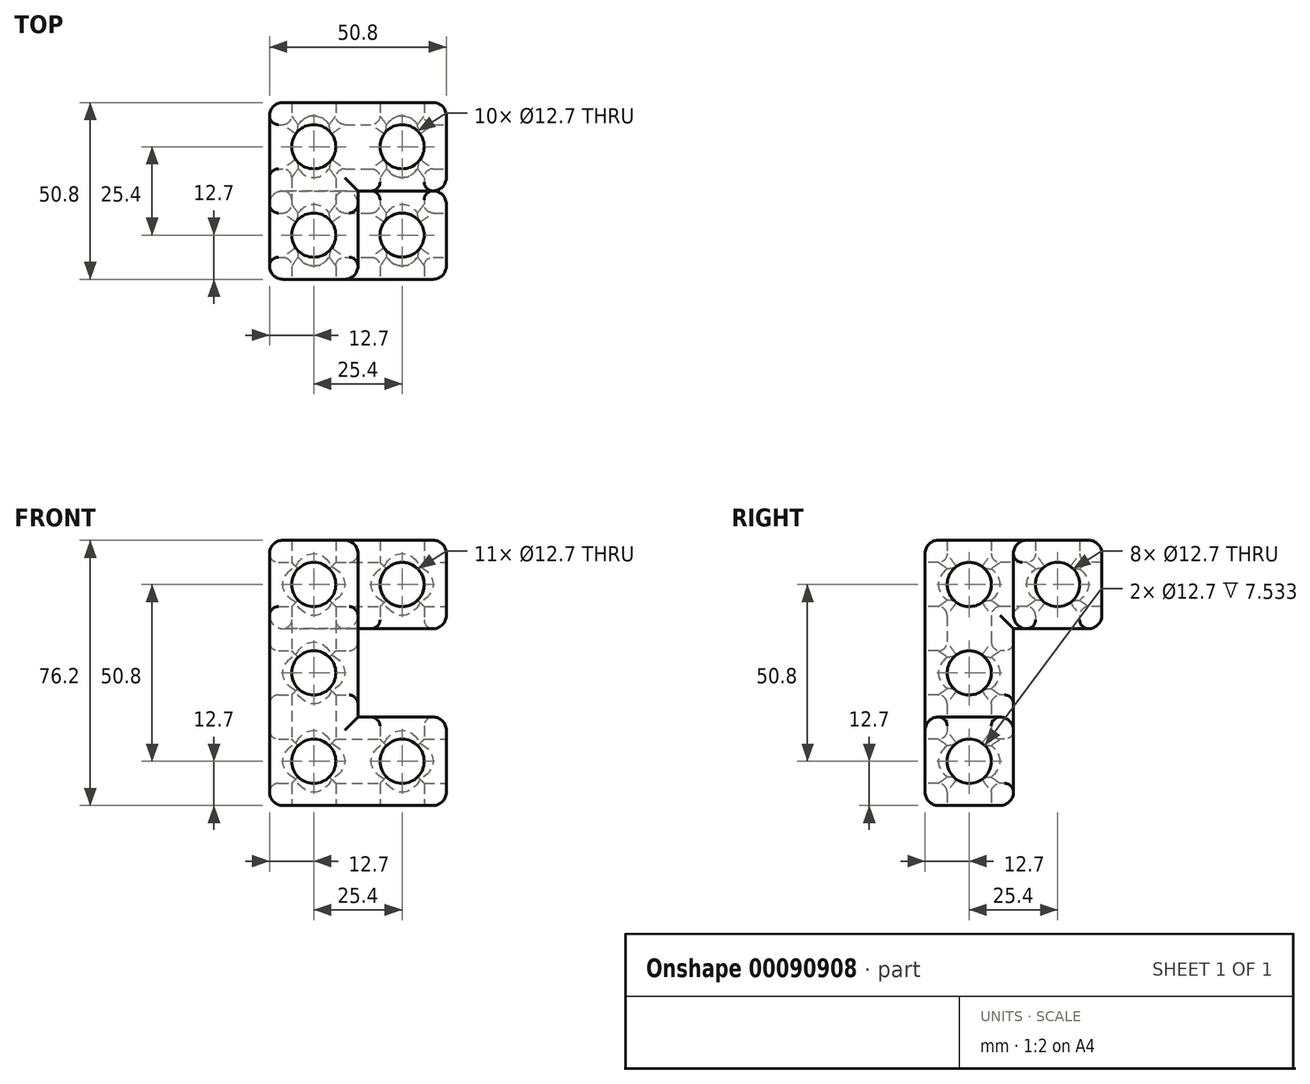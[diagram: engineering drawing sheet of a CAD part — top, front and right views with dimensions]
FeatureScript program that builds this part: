
annotation { "Feature Type Name" : "Feature", "Feature Type Description" : "" }
export const myFeature = defineFeature(function(context is Context, id is Id, definition is map)
    precondition{}
    {
        {
            var Q0;
            Q0=qCreatedBy(makeId("Top.planeOp"),FACE);
            var sketch = newSketch(context, id + "F0", { "sketchPlane" : qUnion([Q0])});
            skLineSegment(sketch, "E0.bottom", {"start": v(0, 0) * mm, "end": v(50.8, 0) * mm});
            skLineSegment(sketch, "E0.top", {"start": v(0, 25.4) * mm, "end": v(50.8, 25.4) * mm});
            skLineSegment(sketch, "E0.left", {"start": v(0, 0) * mm, "end": v(0, 25.4) * mm});
            skLineSegment(sketch, "E0.right", {"start": v(50.8, 0) * mm, "end": v(50.8, 25.4) * mm});
            skSolve(sketch);
        }
        {
            var Q0;
            Q0 = qSketchRegion(id + "F0", true);
            extrude(context, id + "F1", {"entities" : qUnion([Q0]), "depth" : 25.4 * mm});
        }
        {
            var Q0;
            Q0=makeQuery(id+"F1.opExtrude","CAP_FACE",FACE,{"disambiguationData":[OSD([sQuery(id+"F0.wireOp",EDGE,"E0.bottom"),sQuery(id+"F0.wireOp",EDGE,"E0.top"),sQuery(id+"F0.wireOp",EDGE,"E0.left"),sQuery(id+"F0.wireOp",EDGE,"E0.right")])],"isStart":false});
            var sketch = newSketch(context, id + "F2", { "sketchPlane" : qUnion([Q0])});
            skLineSegment(sketch, "E1.bottom", {"start": v(0, 0) * mm, "end": v(25.4, 0) * mm});
            skLineSegment(sketch, "E1.top", {"start": v(0, 25.4) * mm, "end": v(25.4, 25.4) * mm});
            skLineSegment(sketch, "E1.left", {"start": v(0, 0) * mm, "end": v(0, 25.4) * mm});
            skLineSegment(sketch, "E1.right", {"start": v(25.4, 0) * mm, "end": v(25.4, 25.4) * mm});
            skSolve(sketch);
        }
        {
            var Q0;
            Q0 = qSketchRegion(id + "F2", true);
            extrude(context, id + "F3", {"entities" : qUnion([Q0]), "operationType" : NewBodyOperationType.ADD, "depth" : 25.4 * mm});
        }
        {
            var Q0;
            Q0=makeQuery(id+"F3.opExtrude","CAP_FACE",FACE,{"disambiguationData":[OSD([sQuery(id+"F2.wireOp",EDGE,"E1.bottom"),sQuery(id+"F2.wireOp",EDGE,"E1.top"),sQuery(id+"F2.wireOp",EDGE,"E1.left"),sQuery(id+"F2.wireOp",EDGE,"E1.right")])],"isStart":false});
            var sketch = newSketch(context, id + "F4", { "sketchPlane" : qUnion([Q0])});
            skLineSegment(sketch, "E2.left", {"start": v(0, 0) * mm, "end": v(0, 50.8) * mm});
            skLineSegment(sketch, "E3", {"start": v(50.8, 25.4) * mm, "end": v(25.4, 25.4) * mm});
            skLineSegment(sketch, "E4", {"start": v(0, 50.8) * mm, "end": v(18.8, 50.8) * mm});
            skLineSegment(sketch, "E5", {"start": v(18.8, 50.8) * mm, "end": v(50.8, 50.8) * mm});
            skLineSegment(sketch, "E6", {"start": v(50.8, 50.8) * mm, "end": v(50.8, 25.4) * mm});
            skLineSegment(sketch, "E7", {"start": v(25.4, 25.4) * mm, "end": v(25.4, 0) * mm});
            skLineSegment(sketch, "E8", {"start": v(0, 0) * mm, "end": v(25.4, 0) * mm});
            skSolve(sketch);
        }
        {
            var Q0;
            Q0 = qSketchRegion(id + "F4", true);
            extrude(context, id + "F5", {"entities" : qUnion([Q0]), "operationType" : NewBodyOperationType.ADD, "depth" : 25.4 * mm});
        }
        {
            var Q0;
            Q0=makeQuery(id+"F5.boolean.opBoolean","MERGE",FACE,{"derivedFrom":[makeQuery(id+"F3.boolean.opBoolean","MERGE",FACE,{"derivedFrom":[makeQuery(id+"F1.opExtrude","SWEPT_FACE",FACE,{"disambiguationData":[OSD([sQuery(id+"F0.wireOp",EDGE,"E0.bottom")])]}),makeQuery(id+"F3.opExtrude","SWEPT_FACE",FACE,{"disambiguationData":[OSD([sQuery(id+"F2.wireOp",EDGE,"E1.bottom")])]})]}),makeQuery(id+"F5.opExtrude","SWEPT_FACE",FACE,{"disambiguationData":[OSD([sQuery(id+"F4.wireOp",EDGE,"E8")])]})]});
            var sketch = newSketch(context, id + "F6", { "sketchPlane" : qUnion([Q0])});
            skCircle(sketch, "E9", {"center": v(12.7, 63.5) * mm, "radius": 6.35 * mm});
            skLineSegment(sketch, "E10.direction1", {"start": v(12.7, 63.5) * mm, "end": v(38.1, 63.5) * mm, "construction": true});
            skCircle(sketch, "E11.0.1.0", {"center": v(12.7, 38.1) * mm, "radius": 6.35 * mm});
            skCircle(sketch, "E11.0.2.0", {"center": v(12.7, 12.7) * mm, "radius": 6.35 * mm});
            skCircle(sketch, "E11.1.0.0", {"center": v(38.1, 63.5) * mm, "radius": 6.35 * mm});
            skCircle(sketch, "E11.1.1.0", {"center": v(38.1, 38.1) * mm, "radius": 6.35 * mm});
            skCircle(sketch, "E11.1.2.0", {"center": v(38.1, 12.7) * mm, "radius": 6.35 * mm});
            skLineSegment(sketch, "E11.direction2", {"start": v(12.7, 63.5) * mm, "end": v(12.7, 38.1) * mm, "construction": true});
            skSolve(sketch);
        }
        {
            var Q0;
            Q0 = qSketchRegion(id + "F6", true);
            extrude(context, id + "F7", {"entities" : qUnion([Q0]), "operationType" : NewBodyOperationType.REMOVE, "oppositeDirection" : true, "depth" : 50.8 * mm});
        }
        {
            var Q0;
            Q0=makeQuery(id+"F5.opExtrude","SWEPT_FACE",FACE,{"disambiguationData":[OSD([sQuery(id+"F4.wireOp",EDGE,"E6")])]});
            var sketch = newSketch(context, id + "F8", { "sketchPlane" : qUnion([Q0])});
            skCircle(sketch, "E12", {"center": v(12.7, 63.5) * mm, "radius": 6.35 * mm});
            skCircle(sketch, "E13.0.1.0", {"center": v(12.7, 38.1) * mm, "radius": 6.35 * mm});
            skCircle(sketch, "E13.0.2.0", {"center": v(12.7, 12.7) * mm, "radius": 6.35 * mm});
            skCircle(sketch, "E13.1.0.0", {"center": v(38.1, 63.5) * mm, "radius": 6.35 * mm});
            skCircle(sketch, "E13.1.1.0", {"center": v(38.1, 38.1) * mm, "radius": 6.35 * mm});
            skCircle(sketch, "E13.1.2.0", {"center": v(38.1, 12.7) * mm, "radius": 6.35 * mm});
            skLineSegment(sketch, "E13.direction1", {"start": v(12.7, 63.5) * mm, "end": v(38.1, 63.5) * mm, "construction": true});
            skLineSegment(sketch, "E13.direction2", {"start": v(12.7, 63.5) * mm, "end": v(12.7, 38.1) * mm, "construction": true});
            skSolve(sketch);
        }
        {
            var Q0;
            Q0 = qSketchRegion(id + "F8", true);
            extrude(context, id + "F9", {"entities" : qUnion([Q0]), "operationType" : NewBodyOperationType.REMOVE, "oppositeDirection" : true, "depth" : 76.2 * mm});
        }
        {
            var Q0;
            Q0=makeQuery(id+"F1.opExtrude","CAP_FACE",FACE,{"disambiguationData":[OSD([sQuery(id+"F0.wireOp",EDGE,"E0.bottom"),sQuery(id+"F0.wireOp",EDGE,"E0.top"),sQuery(id+"F0.wireOp",EDGE,"E0.left"),sQuery(id+"F0.wireOp",EDGE,"E0.right")])],"isStart":true});
            var sketch = newSketch(context, id + "F10", { "sketchPlane" : qUnion([Q0])});
            skCircle(sketch, "E14", {"center": v(12.7, -12.7) * mm, "radius": 6.35 * mm});
            skCircle(sketch, "E15.0.1.0", {"center": v(12.7, -38.1) * mm, "radius": 6.35 * mm});
            skCircle(sketch, "E15.1.0.0", {"center": v(38.1, -12.7) * mm, "radius": 6.35 * mm});
            skCircle(sketch, "E15.1.1.0", {"center": v(38.1, -38.1) * mm, "radius": 6.35 * mm});
            skLineSegment(sketch, "E15.direction1", {"start": v(12.7, -12.7) * mm, "end": v(38.1, -12.7) * mm, "construction": true});
            skLineSegment(sketch, "E15.direction2", {"start": v(12.7, -12.7) * mm, "end": v(12.7, -38.1) * mm, "construction": true});
            skSolve(sketch);
        }
        {
            var Q0;
            Q0 = qSketchRegion(id + "F10", true);
            extrude(context, id + "F11", {"entities" : qUnion([Q0]), "operationType" : NewBodyOperationType.REMOVE, "oppositeDirection" : true, "depth" : 76.2 * mm});
        }
        {
            var Q0;
            Q0=makeQuery(id+"F11.boolean.opBoolean","COPY",EDGE,{"derivedFrom":makeQuery(id+"F11.opExtrude","CAP_EDGE",EDGE,{"disambiguationData":[OSD([sQuery(id+"F10.wireOp",EDGE,"E15.1.1.0")])],"isStart":false})});
            var Q1;
            Q1=makeQuery(id+"F11.boolean.opBoolean","COPY",EDGE,{"derivedFrom":makeQuery(id+"F11.opExtrude","CAP_EDGE",EDGE,{"disambiguationData":[OSD([sQuery(id+"F10.wireOp",EDGE,"E15.0.1.0")])],"isStart":false})});
            var Q2;
            Q2=makeQuery(id+"F11.boolean.opBoolean","COPY",EDGE,{"derivedFrom":makeQuery(id+"F11.opExtrude","CAP_EDGE",EDGE,{"disambiguationData":[OSD([sQuery(id+"F10.wireOp",EDGE,"E14")])],"isStart":false})});
            var Q3;
            Q3=makeQuery(id+"F11.boolean.opBoolean","INTERSECT",EDGE,{"derivedFrom":[makeQuery(id+"F1.opExtrude","CAP_FACE",FACE,{"disambiguationData":[OSD([sQuery(id+"F0.wireOp",EDGE,"E0.bottom"),sQuery(id+"F0.wireOp",EDGE,"E0.top"),sQuery(id+"F0.wireOp",EDGE,"E0.left"),sQuery(id+"F0.wireOp",EDGE,"E0.right")])],"isStart":false}),makeQuery(id+"F11.opExtrude","SWEPT_FACE",FACE,{"disambiguationData":[OSD([sQuery(id+"F10.wireOp",EDGE,"E15.1.0.0")])]})]});
            var Q4;
            Q4=makeQuery(id+"F9.boolean.opBoolean","INTERSECT",EDGE,{"derivedFrom":[makeQuery(id+"F5.boolean.opBoolean","MERGE",FACE,{"derivedFrom":[makeQuery(id+"F3.opExtrude","SWEPT_FACE",FACE,{"disambiguationData":[OSD([sQuery(id+"F2.wireOp",EDGE,"E1.right")])]}),makeQuery(id+"F5.opExtrude","SWEPT_FACE",FACE,{"disambiguationData":[OSD([sQuery(id+"F4.wireOp",EDGE,"E7")])]})]}),makeQuery(id+"F9.opExtrude","SWEPT_FACE",FACE,{"disambiguationData":[OSD([sQuery(id+"F8.wireOp",EDGE,"E13.0.1.0")])]})]});
            var Q5;
            Q5=makeQuery(id+"F7.boolean.opBoolean","INTERSECT",EDGE,{"derivedFrom":[makeQuery(id+"F5.opExtrude","SWEPT_FACE",FACE,{"disambiguationData":[OSD([sQuery(id+"F4.wireOp",EDGE,"E3")])]}),makeQuery(id+"F7.opExtrude","SWEPT_FACE",FACE,{"disambiguationData":[OSD([sQuery(id+"F6.wireOp",EDGE,"E11.1.0.0")])]})]});
            var Q6;
            Q6=makeQuery(id+"F9.boolean.opBoolean","COPY",EDGE,{"derivedFrom":makeQuery(id+"F9.opExtrude","CAP_EDGE",EDGE,{"disambiguationData":[OSD([sQuery(id+"F8.wireOp",EDGE,"E13.1.0.0")])],"isStart":true})});
            var Q7;
            Q7=makeQuery(id+"F9.boolean.opBoolean","INTERSECT",EDGE,{"derivedFrom":[makeQuery(id+"F5.boolean.opBoolean","MERGE",FACE,{"derivedFrom":[makeQuery(id+"F3.opExtrude","SWEPT_FACE",FACE,{"disambiguationData":[OSD([sQuery(id+"F2.wireOp",EDGE,"E1.right")])]}),makeQuery(id+"F5.opExtrude","SWEPT_FACE",FACE,{"disambiguationData":[OSD([sQuery(id+"F4.wireOp",EDGE,"E7")])]})]}),makeQuery(id+"F9.opExtrude","SWEPT_FACE",FACE,{"disambiguationData":[OSD([sQuery(id+"F8.wireOp",EDGE,"E12")])]})]});
            var Q8;
            Q8=makeQuery(id+"F9.boolean.opBoolean","COPY",EDGE,{"derivedFrom":makeQuery(id+"F9.opExtrude","CAP_EDGE",EDGE,{"disambiguationData":[OSD([sQuery(id+"F8.wireOp",EDGE,"E13.0.2.0")])],"isStart":true})});
            var Q9;
            Q9=makeQuery(id+"F7.boolean.opBoolean","COPY",EDGE,{"derivedFrom":makeQuery(id+"F7.opExtrude","CAP_EDGE",EDGE,{"disambiguationData":[OSD([sQuery(id+"F6.wireOp",EDGE,"E11.0.2.0")])],"isStart":true})});
            var Q10;
            Q10=makeQuery(id+"F7.boolean.opBoolean","COPY",EDGE,{"derivedFrom":makeQuery(id+"F7.opExtrude","CAP_EDGE",EDGE,{"disambiguationData":[OSD([sQuery(id+"F6.wireOp",EDGE,"E11.0.1.0")])],"isStart":true})});
            var Q11;
            Q11=makeQuery(id+"F7.boolean.opBoolean","COPY",EDGE,{"derivedFrom":makeQuery(id+"F7.opExtrude","CAP_EDGE",EDGE,{"disambiguationData":[OSD([sQuery(id+"F6.wireOp",EDGE,"E9")])],"isStart":true})});
            var Q12;
            Q12=makeQuery(id+"F7.boolean.opBoolean","COPY",EDGE,{"derivedFrom":makeQuery(id+"F7.opExtrude","CAP_EDGE",EDGE,{"disambiguationData":[OSD([sQuery(id+"F6.wireOp",EDGE,"E11.1.2.0")])],"isStart":true})});
            var Q13;
            Q13=makeQuery(id+"F9.boolean.opBoolean","INTERSECT",EDGE,{"derivedFrom":[makeQuery(id+"F5.boolean.opBoolean","MERGE",FACE,{"derivedFrom":[makeQuery(id+"F3.boolean.opBoolean","MERGE",FACE,{"derivedFrom":[makeQuery(id+"F1.opExtrude","SWEPT_FACE",FACE,{"disambiguationData":[OSD([sQuery(id+"F0.wireOp",EDGE,"E0.left")])]}),makeQuery(id+"F3.opExtrude","SWEPT_FACE",FACE,{"disambiguationData":[OSD([sQuery(id+"F2.wireOp",EDGE,"E1.left")])]})]}),makeQuery(id+"F5.opExtrude","SWEPT_FACE",FACE,{"disambiguationData":[OSD([sQuery(id+"F4.wireOp",EDGE,"E2.left")])]})]}),makeQuery(id+"F9.opExtrude","SWEPT_FACE",FACE,{"disambiguationData":[OSD([sQuery(id+"F8.wireOp",EDGE,"E12")])]})]});
            var Q14;
            Q14=makeQuery(id+"F9.boolean.opBoolean","INTERSECT",EDGE,{"derivedFrom":[makeQuery(id+"F5.boolean.opBoolean","MERGE",FACE,{"derivedFrom":[makeQuery(id+"F3.boolean.opBoolean","MERGE",FACE,{"derivedFrom":[makeQuery(id+"F1.opExtrude","SWEPT_FACE",FACE,{"disambiguationData":[OSD([sQuery(id+"F0.wireOp",EDGE,"E0.left")])]}),makeQuery(id+"F3.opExtrude","SWEPT_FACE",FACE,{"disambiguationData":[OSD([sQuery(id+"F2.wireOp",EDGE,"E1.left")])]})]}),makeQuery(id+"F5.opExtrude","SWEPT_FACE",FACE,{"disambiguationData":[OSD([sQuery(id+"F4.wireOp",EDGE,"E2.left")])]})]}),makeQuery(id+"F9.opExtrude","SWEPT_FACE",FACE,{"disambiguationData":[OSD([sQuery(id+"F8.wireOp",EDGE,"E13.1.0.0")])]})]});
            var Q15;
            Q15=makeQuery(id+"F11.boolean.opBoolean","INTERSECT",EDGE,{"derivedFrom":[makeQuery(id+"F5.opExtrude","CAP_FACE",FACE,{"disambiguationData":[OSD([sQuery(id+"F4.wireOp",EDGE,"E2.left"),sQuery(id+"F4.wireOp",EDGE,"E3"),sQuery(id+"F4.wireOp",EDGE,"E4"),sQuery(id+"F4.wireOp",EDGE,"E5"),sQuery(id+"F4.wireOp",EDGE,"E6"),sQuery(id+"F4.wireOp",EDGE,"E8"),sQuery(id+"F4.wireOp",EDGE,"E7")])],"isStart":true}),makeQuery(id+"F11.opExtrude","SWEPT_FACE",FACE,{"disambiguationData":[OSD([sQuery(id+"F10.wireOp",EDGE,"E15.0.1.0")])]})]});
            var Q16;
            Q16=makeQuery(id+"F9.boolean.opBoolean","INTERSECT",EDGE,{"derivedFrom":[makeQuery(id+"F5.boolean.opBoolean","MERGE",FACE,{"derivedFrom":[makeQuery(id+"F3.boolean.opBoolean","MERGE",FACE,{"derivedFrom":[makeQuery(id+"F1.opExtrude","SWEPT_FACE",FACE,{"disambiguationData":[OSD([sQuery(id+"F0.wireOp",EDGE,"E0.left")])]}),makeQuery(id+"F3.opExtrude","SWEPT_FACE",FACE,{"disambiguationData":[OSD([sQuery(id+"F2.wireOp",EDGE,"E1.left")])]})]}),makeQuery(id+"F5.opExtrude","SWEPT_FACE",FACE,{"disambiguationData":[OSD([sQuery(id+"F4.wireOp",EDGE,"E2.left")])]})]}),makeQuery(id+"F9.opExtrude","SWEPT_FACE",FACE,{"disambiguationData":[OSD([sQuery(id+"F8.wireOp",EDGE,"E13.0.1.0")])]})]});
            var Q17;
            Q17=makeQuery(id+"F9.boolean.opBoolean","INTERSECT",EDGE,{"derivedFrom":[makeQuery(id+"F5.boolean.opBoolean","MERGE",FACE,{"derivedFrom":[makeQuery(id+"F3.boolean.opBoolean","MERGE",FACE,{"derivedFrom":[makeQuery(id+"F1.opExtrude","SWEPT_FACE",FACE,{"disambiguationData":[OSD([sQuery(id+"F0.wireOp",EDGE,"E0.left")])]}),makeQuery(id+"F3.opExtrude","SWEPT_FACE",FACE,{"disambiguationData":[OSD([sQuery(id+"F2.wireOp",EDGE,"E1.left")])]})]}),makeQuery(id+"F5.opExtrude","SWEPT_FACE",FACE,{"disambiguationData":[OSD([sQuery(id+"F4.wireOp",EDGE,"E2.left")])]})]}),makeQuery(id+"F9.opExtrude","SWEPT_FACE",FACE,{"disambiguationData":[OSD([sQuery(id+"F8.wireOp",EDGE,"E13.0.2.0")])]})]});
            var Q18;
            Q18=makeQuery(id+"F11.boolean.opBoolean","COPY",EDGE,{"derivedFrom":makeQuery(id+"F11.opExtrude","CAP_EDGE",EDGE,{"disambiguationData":[OSD([sQuery(id+"F10.wireOp",EDGE,"E15.1.0.0")])],"isStart":true})});
            var Q19;
            Q19=makeQuery(id+"F11.boolean.opBoolean","COPY",EDGE,{"derivedFrom":makeQuery(id+"F11.opExtrude","CAP_EDGE",EDGE,{"disambiguationData":[OSD([sQuery(id+"F10.wireOp",EDGE,"E14")])],"isStart":true})});
            var Q20;
            Q20=makeQuery(id+"F11.boolean.opBoolean","INTERSECT",EDGE,{"derivedFrom":[makeQuery(id+"F5.opExtrude","CAP_FACE",FACE,{"disambiguationData":[OSD([sQuery(id+"F4.wireOp",EDGE,"E2.left"),sQuery(id+"F4.wireOp",EDGE,"E3"),sQuery(id+"F4.wireOp",EDGE,"E4"),sQuery(id+"F4.wireOp",EDGE,"E5"),sQuery(id+"F4.wireOp",EDGE,"E6"),sQuery(id+"F4.wireOp",EDGE,"E8"),sQuery(id+"F4.wireOp",EDGE,"E7")])],"isStart":true}),makeQuery(id+"F11.opExtrude","SWEPT_FACE",FACE,{"disambiguationData":[OSD([sQuery(id+"F10.wireOp",EDGE,"E15.1.1.0")])]})]});
            var Q21;
            Q21=makeQuery(id+"F7.boolean.opBoolean","COPY",EDGE,{"derivedFrom":makeQuery(id+"F7.opExtrude","CAP_EDGE",EDGE,{"disambiguationData":[OSD([sQuery(id+"F6.wireOp",EDGE,"E9")])],"isStart":false})});
            var Q22;
            Q22=makeQuery(id+"F7.boolean.opBoolean","INTERSECT",EDGE,{"derivedFrom":[makeQuery(id+"F3.boolean.opBoolean","MERGE",FACE,{"derivedFrom":[makeQuery(id+"F1.opExtrude","SWEPT_FACE",FACE,{"disambiguationData":[OSD([sQuery(id+"F0.wireOp",EDGE,"E0.top")])]}),makeQuery(id+"F3.opExtrude","SWEPT_FACE",FACE,{"disambiguationData":[OSD([sQuery(id+"F2.wireOp",EDGE,"E1.top")])]})]}),makeQuery(id+"F7.opExtrude","SWEPT_FACE",FACE,{"disambiguationData":[OSD([sQuery(id+"F6.wireOp",EDGE,"E11.0.1.0")])]})]});
            var Q23;
            Q23=makeQuery(id+"F7.boolean.opBoolean","INTERSECT",EDGE,{"derivedFrom":[makeQuery(id+"F3.boolean.opBoolean","MERGE",FACE,{"derivedFrom":[makeQuery(id+"F1.opExtrude","SWEPT_FACE",FACE,{"disambiguationData":[OSD([sQuery(id+"F0.wireOp",EDGE,"E0.top")])]}),makeQuery(id+"F3.opExtrude","SWEPT_FACE",FACE,{"disambiguationData":[OSD([sQuery(id+"F2.wireOp",EDGE,"E1.top")])]})]}),makeQuery(id+"F7.opExtrude","SWEPT_FACE",FACE,{"disambiguationData":[OSD([sQuery(id+"F6.wireOp",EDGE,"E11.0.2.0")])]})]});
            var Q24;
            Q24=makeQuery(id+"F7.boolean.opBoolean","COPY",EDGE,{"derivedFrom":makeQuery(id+"F7.opExtrude","CAP_EDGE",EDGE,{"disambiguationData":[OSD([sQuery(id+"F6.wireOp",EDGE,"E11.1.0.0")])],"isStart":false})});
            var Q25;
            Q25=makeQuery(id+"F7.boolean.opBoolean","INTERSECT",EDGE,{"derivedFrom":[makeQuery(id+"F3.boolean.opBoolean","MERGE",FACE,{"derivedFrom":[makeQuery(id+"F1.opExtrude","SWEPT_FACE",FACE,{"disambiguationData":[OSD([sQuery(id+"F0.wireOp",EDGE,"E0.top")])]}),makeQuery(id+"F3.opExtrude","SWEPT_FACE",FACE,{"disambiguationData":[OSD([sQuery(id+"F2.wireOp",EDGE,"E1.top")])]})]}),makeQuery(id+"F7.opExtrude","SWEPT_FACE",FACE,{"disambiguationData":[OSD([sQuery(id+"F6.wireOp",EDGE,"E11.1.2.0")])]})]});
            fillet(context, id + "F12", {"entities" : qUnion([Q0, Q1, Q2, Q3, Q4, Q5, Q6, Q7, Q8, Q9, Q10, Q11, Q12, Q13, Q14, Q15, Q16, Q17, Q18, Q19, Q20, Q21, Q22, Q23, Q24, Q25]), "radius" : 2.54 * mm, "tangentPropagation" : true, "allowEdgeOverflow" : false});
        }
        {
            var Q0;
            Q0=makeQuery(id+"F5.boolean.opBoolean","MERGE",EDGE,{"derivedFrom":[makeQuery(id+"F3.boolean.opBoolean","MERGE",EDGE,{"derivedFrom":[makeQuery(id+"F1.opExtrude","SWEPT_EDGE",EDGE,{"disambiguationData":[OSD([sQuery(id+"F0.wireOp",EDGE,"E0.bottom"),sQuery(id+"F0.wireOp",EDGE,"E0.left")])]}),makeQuery(id+"F3.opExtrude","SWEPT_EDGE",EDGE,{"disambiguationData":[OSD([sQuery(id+"F2.wireOp",EDGE,"E1.bottom"),sQuery(id+"F2.wireOp",EDGE,"E1.left")])]})]}),makeQuery(id+"F5.opExtrude","SWEPT_EDGE",EDGE,{"disambiguationData":[OSD([sQuery(id+"F4.wireOp",EDGE,"E2.left"),sQuery(id+"F4.wireOp",EDGE,"E8")])]})]});
            var Q1;
            Q1=makeQuery(id+"F5.opExtrude","CAP_EDGE",EDGE,{"disambiguationData":[OSD([sQuery(id+"F4.wireOp",EDGE,"E8")])],"isStart":false});
            var Q2;
            Q2=makeQuery(id+"F5.boolean.opBoolean","MERGE",EDGE,{"derivedFrom":[makeQuery(id+"F3.opExtrude","SWEPT_EDGE",EDGE,{"disambiguationData":[OSD([sQuery(id+"F0.wireOp",EDGE,"E0.bottom"),sQuery(id+"F2.wireOp",EDGE,"E1.bottom"),sQuery(id+"F2.wireOp",EDGE,"E1.right")])]}),makeQuery(id+"F5.opExtrude","SWEPT_EDGE",EDGE,{"disambiguationData":[OSD([sQuery(id+"F4.wireOp",EDGE,"E8"),sQuery(id+"F4.wireOp",EDGE,"E7")])]})]});
            var Q3;
            Q3=makeQuery(id+"F1.opExtrude","CAP_EDGE",EDGE,{"disambiguationData":[OSD([sQuery(id+"F0.wireOp",EDGE,"E0.bottom")])],"isStart":false});
            var Q4;
            Q4=makeQuery(id+"F1.opExtrude","SWEPT_EDGE",EDGE,{"disambiguationData":[OSD([sQuery(id+"F0.wireOp",EDGE,"E0.bottom"),sQuery(id+"F0.wireOp",EDGE,"E0.right")])]});
            var Q5;
            Q5=makeQuery(id+"F1.opExtrude","CAP_EDGE",EDGE,{"disambiguationData":[OSD([sQuery(id+"F0.wireOp",EDGE,"E0.bottom")])],"isStart":true});
            var Q6;
            Q6=makeQuery(id+"F1.opExtrude","CAP_EDGE",EDGE,{"disambiguationData":[OSD([sQuery(id+"F0.wireOp",EDGE,"E0.right")])],"isStart":true});
            var Q7;
            Q7=makeQuery(id+"F1.opExtrude","CAP_EDGE",EDGE,{"disambiguationData":[OSD([sQuery(id+"F0.wireOp",EDGE,"E0.top")])],"isStart":true});
            var Q8;
            Q8=makeQuery(id+"F1.opExtrude","CAP_EDGE",EDGE,{"disambiguationData":[OSD([sQuery(id+"F0.wireOp",EDGE,"E0.left")])],"isStart":true});
            var Q9;
            Q9=makeQuery(id+"F3.boolean.opBoolean","MERGE",EDGE,{"derivedFrom":[makeQuery(id+"F1.opExtrude","SWEPT_EDGE",EDGE,{"disambiguationData":[OSD([sQuery(id+"F0.wireOp",EDGE,"E0.top"),sQuery(id+"F0.wireOp",EDGE,"E0.left")])]}),makeQuery(id+"F3.opExtrude","SWEPT_EDGE",EDGE,{"disambiguationData":[OSD([sQuery(id+"F2.wireOp",EDGE,"E1.top"),sQuery(id+"F2.wireOp",EDGE,"E1.left")])]})]});
            var Q10;
            Q10=makeQuery(id+"F5.opExtrude","CAP_EDGE",EDGE,{"disambiguationData":[OSD([sQuery(id+"F4.wireOp",EDGE,"E2.left")])],"isStart":false});
            var Q11;
            Q11=makeQuery(id+"F5.opExtrude","SWEPT_EDGE",EDGE,{"disambiguationData":[OSD([sQuery(id+"F4.wireOp",EDGE,"E2.left"),sQuery(id+"F4.wireOp",EDGE,"E4")])]});
            var Q12;
            Q12=makeQuery(id+"F5.opExtrude","CAP_EDGE",EDGE,{"disambiguationData":[OSD([sQuery(id+"F4.wireOp",EDGE,"E4"),sQuery(id+"F4.wireOp",EDGE,"E5")])],"isStart":true});
            var Q13;
            Q13=makeQuery(id+"F5.opExtrude","CAP_EDGE",EDGE,{"disambiguationData":[OSD([sQuery(id+"F4.wireOp",EDGE,"E2.left")])],"isStart":true});
            var Q14;
            Q14=makeQuery(id+"F1.opExtrude","CAP_EDGE",EDGE,{"disambiguationData":[OSD([sQuery(id+"F0.wireOp",EDGE,"E0.right")])],"isStart":false});
            var Q15;
            Q15=makeQuery(id+"F1.opExtrude","SWEPT_EDGE",EDGE,{"disambiguationData":[OSD([sQuery(id+"F0.wireOp",EDGE,"E0.top"),sQuery(id+"F0.wireOp",EDGE,"E0.right")])]});
            var Q16;
            Q16=makeQuery(id+"F1.opExtrude","CAP_EDGE",EDGE,{"disambiguationData":[OSD([sQuery(id+"F0.wireOp",EDGE,"E0.top")])],"isStart":false});
            var Q17;
            Q17=makeQuery(id+"F3.opExtrude","SWEPT_EDGE",EDGE,{"disambiguationData":[OSD([sQuery(id+"F0.wireOp",EDGE,"E0.top"),sQuery(id+"F2.wireOp",EDGE,"E1.top"),sQuery(id+"F2.wireOp",EDGE,"E1.right")])]});
            var Q18;
            Q18=makeQuery(id+"F5.opExtrude","SWEPT_EDGE",EDGE,{"disambiguationData":[OSD([sQuery(id+"F4.wireOp",EDGE,"E5"),sQuery(id+"F4.wireOp",EDGE,"E6")])]});
            var Q19;
            Q19=makeQuery(id+"F5.opExtrude","CAP_EDGE",EDGE,{"disambiguationData":[OSD([sQuery(id+"F4.wireOp",EDGE,"E4"),sQuery(id+"F4.wireOp",EDGE,"E5")])],"isStart":false});
            var Q20;
            Q20=makeQuery(id+"F5.opExtrude","CAP_EDGE",EDGE,{"disambiguationData":[OSD([sQuery(id+"F4.wireOp",EDGE,"E6")])],"isStart":false});
            var Q21;
            Q21=makeQuery(id+"F5.opExtrude","CAP_EDGE",EDGE,{"disambiguationData":[OSD([sQuery(id+"F4.wireOp",EDGE,"E7")])],"isStart":false});
            var Q22;
            Q22=makeQuery(id+"F5.opExtrude","CAP_EDGE",EDGE,{"disambiguationData":[OSD([sQuery(id+"F4.wireOp",EDGE,"E3")])],"isStart":false});
            var Q23;
            Q23=makeQuery(id+"F5.opExtrude","SWEPT_EDGE",EDGE,{"disambiguationData":[OSD([sQuery(id+"F4.wireOp",EDGE,"E3"),sQuery(id+"F4.wireOp",EDGE,"E6")])]});
            var Q24;
            Q24=makeQuery(id+"F5.opExtrude","CAP_EDGE",EDGE,{"disambiguationData":[OSD([sQuery(id+"F4.wireOp",EDGE,"E6")])],"isStart":true});
            fillet(context, id + "F13", {"entities" : qUnion([Q0, Q1, Q2, Q3, Q4, Q5, Q6, Q7, Q8, Q9, Q10, Q11, Q12, Q13, Q14, Q15, Q16, Q17, Q18, Q19, Q20, Q21, Q22, Q23, Q24]), "radius" : 3.8 * mm, "tangentPropagation" : true, "allowEdgeOverflow" : false});
        }
        {
            var Q0;
            Q0=makeQuery(id+"F5.opExtrude","CAP_EDGE",EDGE,{"disambiguationData":[OSD([sQuery(id+"F4.wireOp",EDGE,"E3")])],"isStart":true});
            var Q1;
            {var subQ0=sQuery(id+"F2.wireOp",EDGE,"E1.top");Q1=makeQuery(id+"F13.opFillet","TWEAK_EDGE",EDGE,{"derivedFrom":[makeQuery(id+"F5.boolean.opBoolean","MERGE",VERTEX,{"derivedFrom":[makeQuery(id+"F3.opExtrude","CAP_VERTEX",VERTEX,{"disambiguationData":[OSD([sQuery(id+"F0.wireOp",EDGE,"E0.top"),subQ0,sQuery(id+"F2.wireOp",EDGE,"E1.right")])],"isStart":false}),makeQuery(id+"F5.opExtrude","CAP_VERTEX",VERTEX,{"disambiguationData":[OSD([subQ0,sQuery(id+"F4.wireOp",EDGE,"E3"),sQuery(id+"F4.wireOp",EDGE,"E7")])],"isStart":true})]})]});}
            fillet(context, id + "F14", {"entities" : qUnion([Q0, Q1]), "radius" : 3.8 * mm, "tangentPropagation" : true, "allowEdgeOverflow" : false});
        }
        {
            var Q0;
            Q0=makeQuery(id+"F11.boolean.opBoolean","INTERSECT",EDGE,{"disambiguationData":[OD(0.0)],"derivedFrom":[makeQuery(id+"F9.boolean.opBoolean","COPY",FACE,{"disambiguationData":[OD(2.0)],"derivedFrom":makeQuery(id+"F9.opExtrude","SWEPT_FACE",FACE,{"disambiguationData":[OSD([sQuery(id+"F8.wireOp",EDGE,"E13.0.2.0")])]})}),makeQuery(id+"F11.opExtrude","SWEPT_FACE",FACE,{"disambiguationData":[OSD([sQuery(id+"F10.wireOp",EDGE,"E15.1.0.0")])]})]});
            var Q1;
            Q1=makeQuery(id+"F9.boolean.opBoolean","INTERSECT",EDGE,{"disambiguationData":[OD(1.0)],"derivedFrom":[makeQuery(id+"F7.boolean.opBoolean","COPY",FACE,{"derivedFrom":makeQuery(id+"F7.opExtrude","SWEPT_FACE",FACE,{"disambiguationData":[OSD([sQuery(id+"F6.wireOp",EDGE,"E11.1.2.0")])]})}),makeQuery(id+"F9.opExtrude","SWEPT_FACE",FACE,{"disambiguationData":[OSD([sQuery(id+"F8.wireOp",EDGE,"E13.0.2.0")])]})]});
            var Q2;
            {var subQ0=makeQuery(id+"F7.boolean.opBoolean","COPY",FACE,{"derivedFrom":makeQuery(id+"F7.opExtrude","SWEPT_FACE",FACE,{"disambiguationData":[OSD([sQuery(id+"F6.wireOp",EDGE,"E11.1.2.0")])]})});Q2=makeQuery(id+"F11.boolean.opBoolean","INTERSECT",EDGE,{"disambiguationData":[OD(0.0)],"derivedFrom":[makeQuery(id+"F9.boolean.opBoolean","SPLIT",FACE,{"disambiguationData":[TD([makeQuery(id+"F1.opExtrude","SWEPT_FACE",FACE,{"disambiguationData":[OSD([sQuery(id+"F0.wireOp",EDGE,"E0.bottom")])]})])],"derivedFrom":subQ0}),makeQuery(id+"F11.opExtrude","SWEPT_FACE",FACE,{"disambiguationData":[OSD([sQuery(id+"F10.wireOp",EDGE,"E15.1.0.0")])]})]});}
            var Q3;
            {var subQ0=makeQuery(id+"F7.boolean.opBoolean","COPY",FACE,{"derivedFrom":makeQuery(id+"F7.opExtrude","SWEPT_FACE",FACE,{"disambiguationData":[OSD([sQuery(id+"F6.wireOp",EDGE,"E11.1.2.0")])]})});Q3=makeQuery(id+"F11.boolean.opBoolean","INTERSECT",EDGE,{"disambiguationData":[OD(1.0)],"derivedFrom":[makeQuery(id+"F9.boolean.opBoolean","SPLIT",FACE,{"disambiguationData":[TD([makeQuery(id+"F1.opExtrude","SWEPT_FACE",FACE,{"disambiguationData":[OSD([sQuery(id+"F0.wireOp",EDGE,"E0.top")])]})])],"derivedFrom":subQ0}),makeQuery(id+"F11.opExtrude","SWEPT_FACE",FACE,{"disambiguationData":[OSD([sQuery(id+"F10.wireOp",EDGE,"E15.1.0.0")])]})]});}
            var Q4;
            Q4=makeQuery(id+"F11.boolean.opBoolean","INTERSECT",EDGE,{"disambiguationData":[OD(1.0)],"derivedFrom":[makeQuery(id+"F9.boolean.opBoolean","COPY",FACE,{"disambiguationData":[OD(2.0)],"derivedFrom":makeQuery(id+"F9.opExtrude","SWEPT_FACE",FACE,{"disambiguationData":[OSD([sQuery(id+"F8.wireOp",EDGE,"E13.0.2.0")])]})}),makeQuery(id+"F11.opExtrude","SWEPT_FACE",FACE,{"disambiguationData":[OSD([sQuery(id+"F10.wireOp",EDGE,"E15.1.0.0")])]})]});
            var Q5;
            Q5=makeQuery(id+"F11.boolean.opBoolean","INTERSECT",EDGE,{"disambiguationData":[OD(0.0)],"derivedFrom":[makeQuery(id+"F9.boolean.opBoolean","COPY",FACE,{"disambiguationData":[OD(1.0)],"derivedFrom":makeQuery(id+"F9.opExtrude","SWEPT_FACE",FACE,{"disambiguationData":[OSD([sQuery(id+"F8.wireOp",EDGE,"E13.0.2.0")])]})}),makeQuery(id+"F11.opExtrude","SWEPT_FACE",FACE,{"disambiguationData":[OSD([sQuery(id+"F10.wireOp",EDGE,"E14")])]})]});
            var Q6;
            Q6=makeQuery(id+"F9.boolean.opBoolean","INTERSECT",EDGE,{"disambiguationData":[OD(0.0)],"derivedFrom":[makeQuery(id+"F7.boolean.opBoolean","COPY",FACE,{"derivedFrom":makeQuery(id+"F7.opExtrude","SWEPT_FACE",FACE,{"disambiguationData":[OSD([sQuery(id+"F6.wireOp",EDGE,"E11.0.2.0")])]})}),makeQuery(id+"F9.opExtrude","SWEPT_FACE",FACE,{"disambiguationData":[OSD([sQuery(id+"F8.wireOp",EDGE,"E13.0.2.0")])]})]});
            var Q7;
            {var subQ0=makeQuery(id+"F7.boolean.opBoolean","COPY",FACE,{"derivedFrom":makeQuery(id+"F7.opExtrude","SWEPT_FACE",FACE,{"disambiguationData":[OSD([sQuery(id+"F6.wireOp",EDGE,"E11.0.2.0")])]})});Q7=makeQuery(id+"F11.boolean.opBoolean","INTERSECT",EDGE,{"disambiguationData":[OD(0.0)],"derivedFrom":[makeQuery(id+"F9.boolean.opBoolean","SPLIT",FACE,{"disambiguationData":[TD([makeQuery(id+"F1.opExtrude","SWEPT_FACE",FACE,{"disambiguationData":[OSD([sQuery(id+"F0.wireOp",EDGE,"E0.bottom")])]})])],"derivedFrom":subQ0}),makeQuery(id+"F11.opExtrude","SWEPT_FACE",FACE,{"disambiguationData":[OSD([sQuery(id+"F10.wireOp",EDGE,"E14")])]})]});}
            var Q8;
            Q8=makeQuery(id+"F9.boolean.opBoolean","INTERSECT",EDGE,{"disambiguationData":[OD(1.0)],"derivedFrom":[makeQuery(id+"F7.boolean.opBoolean","COPY",FACE,{"derivedFrom":makeQuery(id+"F7.opExtrude","SWEPT_FACE",FACE,{"disambiguationData":[OSD([sQuery(id+"F6.wireOp",EDGE,"E11.0.1.0")])]})}),makeQuery(id+"F9.opExtrude","SWEPT_FACE",FACE,{"disambiguationData":[OSD([sQuery(id+"F8.wireOp",EDGE,"E13.0.1.0")])]})]});
            var Q9;
            Q9=makeQuery(id+"F11.boolean.opBoolean","INTERSECT",EDGE,{"disambiguationData":[OD(1.0)],"derivedFrom":[makeQuery(id+"F9.boolean.opBoolean","COPY",FACE,{"disambiguationData":[OD(1.0)],"derivedFrom":makeQuery(id+"F9.opExtrude","SWEPT_FACE",FACE,{"disambiguationData":[OSD([sQuery(id+"F8.wireOp",EDGE,"E13.0.1.0")])]})}),makeQuery(id+"F11.opExtrude","SWEPT_FACE",FACE,{"disambiguationData":[OSD([sQuery(id+"F10.wireOp",EDGE,"E14")])]})]});
            var Q10;
            {var subQ0=makeQuery(id+"F7.boolean.opBoolean","COPY",FACE,{"derivedFrom":makeQuery(id+"F7.opExtrude","SWEPT_FACE",FACE,{"disambiguationData":[OSD([sQuery(id+"F6.wireOp",EDGE,"E11.0.1.0")])]})});Q10=makeQuery(id+"F11.boolean.opBoolean","INTERSECT",EDGE,{"disambiguationData":[OD(1.0)],"derivedFrom":[makeQuery(id+"F9.boolean.opBoolean","SPLIT",FACE,{"disambiguationData":[TD([makeQuery(id+"F1.opExtrude","SWEPT_FACE",FACE,{"disambiguationData":[OSD([sQuery(id+"F0.wireOp",EDGE,"E0.bottom")])]})])],"derivedFrom":subQ0}),makeQuery(id+"F11.opExtrude","SWEPT_FACE",FACE,{"disambiguationData":[OSD([sQuery(id+"F10.wireOp",EDGE,"E14")])]})]});}
            var Q11;
            Q11=makeQuery(id+"F9.boolean.opBoolean","INTERSECT",EDGE,{"disambiguationData":[OD(3.0)],"derivedFrom":[makeQuery(id+"F7.boolean.opBoolean","COPY",FACE,{"derivedFrom":makeQuery(id+"F7.opExtrude","SWEPT_FACE",FACE,{"disambiguationData":[OSD([sQuery(id+"F6.wireOp",EDGE,"E11.1.2.0")])]})}),makeQuery(id+"F9.opExtrude","SWEPT_FACE",FACE,{"disambiguationData":[OSD([sQuery(id+"F8.wireOp",EDGE,"E13.0.2.0")])]})]});
            var Q12;
            {var subQ0=makeQuery(id+"F7.boolean.opBoolean","COPY",FACE,{"derivedFrom":makeQuery(id+"F7.opExtrude","SWEPT_FACE",FACE,{"disambiguationData":[OSD([sQuery(id+"F6.wireOp",EDGE,"E11.1.2.0")])]})});Q12=makeQuery(id+"F11.boolean.opBoolean","INTERSECT",EDGE,{"disambiguationData":[OD(0.0)],"derivedFrom":[makeQuery(id+"F9.boolean.opBoolean","SPLIT",FACE,{"disambiguationData":[TD([makeQuery(id+"F1.opExtrude","SWEPT_FACE",FACE,{"disambiguationData":[OSD([sQuery(id+"F0.wireOp",EDGE,"E0.top")])]})])],"derivedFrom":subQ0}),makeQuery(id+"F11.opExtrude","SWEPT_FACE",FACE,{"disambiguationData":[OSD([sQuery(id+"F10.wireOp",EDGE,"E15.1.0.0")])]})]});}
            var Q13;
            Q13=makeQuery(id+"F11.boolean.opBoolean","INTERSECT",EDGE,{"disambiguationData":[OD(0.0)],"derivedFrom":[makeQuery(id+"F9.boolean.opBoolean","COPY",FACE,{"disambiguationData":[OD(0.0)],"derivedFrom":makeQuery(id+"F9.opExtrude","SWEPT_FACE",FACE,{"disambiguationData":[OSD([sQuery(id+"F8.wireOp",EDGE,"E13.0.2.0")])]})}),makeQuery(id+"F11.opExtrude","SWEPT_FACE",FACE,{"disambiguationData":[OSD([sQuery(id+"F10.wireOp",EDGE,"E15.1.0.0")])]})]});
            var Q14;
            Q14=makeQuery(id+"F9.boolean.opBoolean","INTERSECT",EDGE,{"disambiguationData":[OD(2.0)],"derivedFrom":[makeQuery(id+"F7.boolean.opBoolean","COPY",FACE,{"derivedFrom":makeQuery(id+"F7.opExtrude","SWEPT_FACE",FACE,{"disambiguationData":[OSD([sQuery(id+"F6.wireOp",EDGE,"E11.1.2.0")])]})}),makeQuery(id+"F9.opExtrude","SWEPT_FACE",FACE,{"disambiguationData":[OSD([sQuery(id+"F8.wireOp",EDGE,"E13.0.2.0")])]})]});
            var Q15;
            {var subQ0=makeQuery(id+"F7.boolean.opBoolean","COPY",FACE,{"derivedFrom":makeQuery(id+"F7.opExtrude","SWEPT_FACE",FACE,{"disambiguationData":[OSD([sQuery(id+"F6.wireOp",EDGE,"E11.1.2.0")])]})});Q15=makeQuery(id+"F11.boolean.opBoolean","INTERSECT",EDGE,{"disambiguationData":[OD(1.0)],"derivedFrom":[makeQuery(id+"F9.boolean.opBoolean","SPLIT",FACE,{"disambiguationData":[TD([makeQuery(id+"F1.opExtrude","SWEPT_FACE",FACE,{"disambiguationData":[OSD([sQuery(id+"F0.wireOp",EDGE,"E0.bottom")])]})])],"derivedFrom":subQ0}),makeQuery(id+"F11.opExtrude","SWEPT_FACE",FACE,{"disambiguationData":[OSD([sQuery(id+"F10.wireOp",EDGE,"E15.1.0.0")])]})]});}
            var Q16;
            Q16=makeQuery(id+"F11.boolean.opBoolean","INTERSECT",EDGE,{"disambiguationData":[OD(1.0)],"derivedFrom":[makeQuery(id+"F9.boolean.opBoolean","COPY",FACE,{"disambiguationData":[OD(0.0)],"derivedFrom":makeQuery(id+"F9.opExtrude","SWEPT_FACE",FACE,{"disambiguationData":[OSD([sQuery(id+"F8.wireOp",EDGE,"E13.0.2.0")])]})}),makeQuery(id+"F11.opExtrude","SWEPT_FACE",FACE,{"disambiguationData":[OSD([sQuery(id+"F10.wireOp",EDGE,"E15.1.0.0")])]})]});
            var Q17;
            Q17=makeQuery(id+"F9.boolean.opBoolean","INTERSECT",EDGE,{"disambiguationData":[OD(0.0)],"derivedFrom":[makeQuery(id+"F7.boolean.opBoolean","COPY",FACE,{"derivedFrom":makeQuery(id+"F7.opExtrude","SWEPT_FACE",FACE,{"disambiguationData":[OSD([sQuery(id+"F6.wireOp",EDGE,"E11.1.2.0")])]})}),makeQuery(id+"F9.opExtrude","SWEPT_FACE",FACE,{"disambiguationData":[OSD([sQuery(id+"F8.wireOp",EDGE,"E13.0.2.0")])]})]});
            var Q18;
            Q18=makeQuery(id+"F9.boolean.opBoolean","INTERSECT",EDGE,{"disambiguationData":[OD(2.0)],"derivedFrom":[makeQuery(id+"F7.boolean.opBoolean","COPY",FACE,{"derivedFrom":makeQuery(id+"F7.opExtrude","SWEPT_FACE",FACE,{"disambiguationData":[OSD([sQuery(id+"F6.wireOp",EDGE,"E9")])]})}),makeQuery(id+"F9.opExtrude","SWEPT_FACE",FACE,{"disambiguationData":[OSD([sQuery(id+"F8.wireOp",EDGE,"E12")])]})]});
            var Q19;
            Q19=makeQuery(id+"F11.boolean.opBoolean","INTERSECT",EDGE,{"disambiguationData":[OD(1.0)],"derivedFrom":[makeQuery(id+"F9.boolean.opBoolean","COPY",FACE,{"disambiguationData":[OD(0.0)],"derivedFrom":makeQuery(id+"F9.opExtrude","SWEPT_FACE",FACE,{"disambiguationData":[OSD([sQuery(id+"F8.wireOp",EDGE,"E12")])]})}),makeQuery(id+"F11.opExtrude","SWEPT_FACE",FACE,{"disambiguationData":[OSD([sQuery(id+"F10.wireOp",EDGE,"E14")])]})]});
            var Q20;
            {var subQ0=makeQuery(id+"F7.boolean.opBoolean","COPY",FACE,{"derivedFrom":makeQuery(id+"F7.opExtrude","SWEPT_FACE",FACE,{"disambiguationData":[OSD([sQuery(id+"F6.wireOp",EDGE,"E9")])]})});Q20=makeQuery(id+"F11.boolean.opBoolean","INTERSECT",EDGE,{"disambiguationData":[OD(1.0)],"derivedFrom":[makeQuery(id+"F9.boolean.opBoolean","SPLIT",FACE,{"disambiguationData":[TD([subQ0,makeQuery(id+"F9.opExtrude","SWEPT_FACE",FACE,{"disambiguationData":[OSD([sQuery(id+"F8.wireOp",EDGE,"E12")])]}),makeQuery(id+"F9.opExtrude","SWEPT_FACE",FACE,{"disambiguationData":[OSD([sQuery(id+"F8.wireOp",EDGE,"E13.1.0.0")])]})])],"derivedFrom":subQ0}),makeQuery(id+"F11.opExtrude","SWEPT_FACE",FACE,{"disambiguationData":[OSD([sQuery(id+"F10.wireOp",EDGE,"E14")])]})]});}
            var Q21;
            Q21=makeQuery(id+"F11.boolean.opBoolean","INTERSECT",EDGE,{"disambiguationData":[OD(1.0)],"derivedFrom":[makeQuery(id+"F9.boolean.opBoolean","COPY",FACE,{"disambiguationData":[OD(2.0)],"derivedFrom":makeQuery(id+"F9.opExtrude","SWEPT_FACE",FACE,{"disambiguationData":[OSD([sQuery(id+"F8.wireOp",EDGE,"E13.1.0.0")])]})}),makeQuery(id+"F11.opExtrude","SWEPT_FACE",FACE,{"disambiguationData":[OSD([sQuery(id+"F10.wireOp",EDGE,"E15.0.1.0")])]})]});
            var Q22;
            {var subQ0=makeQuery(id+"F7.boolean.opBoolean","COPY",FACE,{"derivedFrom":makeQuery(id+"F7.opExtrude","SWEPT_FACE",FACE,{"disambiguationData":[OSD([sQuery(id+"F6.wireOp",EDGE,"E9")])]})});Q22=makeQuery(id+"F11.boolean.opBoolean","INTERSECT",EDGE,{"disambiguationData":[OD(1.0)],"derivedFrom":[makeQuery(id+"F9.boolean.opBoolean","SPLIT",FACE,{"disambiguationData":[TD([makeQuery(id+"F5.opExtrude","SWEPT_FACE",FACE,{"disambiguationData":[OSD([sQuery(id+"F4.wireOp",EDGE,"E4"),sQuery(id+"F4.wireOp",EDGE,"E5")])]}),subQ0,makeQuery(id+"F9.opExtrude","SWEPT_FACE",FACE,{"disambiguationData":[OSD([sQuery(id+"F8.wireOp",EDGE,"E13.1.0.0")])]})])],"derivedFrom":subQ0}),makeQuery(id+"F11.opExtrude","SWEPT_FACE",FACE,{"disambiguationData":[OSD([sQuery(id+"F10.wireOp",EDGE,"E15.0.1.0")])]})]});}
            var Q23;
            Q23=makeQuery(id+"F9.boolean.opBoolean","INTERSECT",EDGE,{"disambiguationData":[OD(1.0)],"derivedFrom":[makeQuery(id+"F7.boolean.opBoolean","COPY",FACE,{"derivedFrom":makeQuery(id+"F7.opExtrude","SWEPT_FACE",FACE,{"disambiguationData":[OSD([sQuery(id+"F6.wireOp",EDGE,"E9")])]})}),makeQuery(id+"F9.opExtrude","SWEPT_FACE",FACE,{"disambiguationData":[OSD([sQuery(id+"F8.wireOp",EDGE,"E13.1.0.0")])]})]});
            var Q24;
            Q24=makeQuery(id+"F11.boolean.opBoolean","INTERSECT",EDGE,{"disambiguationData":[OD(0.0)],"derivedFrom":[makeQuery(id+"F9.boolean.opBoolean","COPY",FACE,{"disambiguationData":[OD(0.0)],"derivedFrom":makeQuery(id+"F9.opExtrude","SWEPT_FACE",FACE,{"disambiguationData":[OSD([sQuery(id+"F8.wireOp",EDGE,"E12")])]})}),makeQuery(id+"F11.opExtrude","SWEPT_FACE",FACE,{"disambiguationData":[OSD([sQuery(id+"F10.wireOp",EDGE,"E14")])]})]});
            var Q25;
            {var subQ0=makeQuery(id+"F7.boolean.opBoolean","COPY",FACE,{"derivedFrom":makeQuery(id+"F7.opExtrude","SWEPT_FACE",FACE,{"disambiguationData":[OSD([sQuery(id+"F6.wireOp",EDGE,"E9")])]})});Q25=makeQuery(id+"F11.boolean.opBoolean","INTERSECT",EDGE,{"disambiguationData":[OD(0.0)],"derivedFrom":[makeQuery(id+"F9.boolean.opBoolean","SPLIT",FACE,{"disambiguationData":[TD([subQ0,makeQuery(id+"F9.opExtrude","SWEPT_FACE",FACE,{"disambiguationData":[OSD([sQuery(id+"F8.wireOp",EDGE,"E12")])]}),makeQuery(id+"F9.opExtrude","SWEPT_FACE",FACE,{"disambiguationData":[OSD([sQuery(id+"F8.wireOp",EDGE,"E13.1.0.0")])]})])],"derivedFrom":subQ0}),makeQuery(id+"F11.opExtrude","SWEPT_FACE",FACE,{"disambiguationData":[OSD([sQuery(id+"F10.wireOp",EDGE,"E14")])]})]});}
            var Q26;
            Q26=makeQuery(id+"F11.boolean.opBoolean","INTERSECT",EDGE,{"disambiguationData":[OD(0.0)],"derivedFrom":[makeQuery(id+"F9.boolean.opBoolean","COPY",FACE,{"disambiguationData":[OD(2.0)],"derivedFrom":makeQuery(id+"F9.opExtrude","SWEPT_FACE",FACE,{"disambiguationData":[OSD([sQuery(id+"F8.wireOp",EDGE,"E13.1.0.0")])]})}),makeQuery(id+"F11.opExtrude","SWEPT_FACE",FACE,{"disambiguationData":[OSD([sQuery(id+"F10.wireOp",EDGE,"E15.0.1.0")])]})]});
            var Q27;
            {var subQ0=makeQuery(id+"F7.boolean.opBoolean","COPY",FACE,{"derivedFrom":makeQuery(id+"F7.opExtrude","SWEPT_FACE",FACE,{"disambiguationData":[OSD([sQuery(id+"F6.wireOp",EDGE,"E9")])]})});Q27=makeQuery(id+"F11.boolean.opBoolean","INTERSECT",EDGE,{"disambiguationData":[OD(0.0)],"derivedFrom":[makeQuery(id+"F9.boolean.opBoolean","SPLIT",FACE,{"disambiguationData":[TD([makeQuery(id+"F5.opExtrude","SWEPT_FACE",FACE,{"disambiguationData":[OSD([sQuery(id+"F4.wireOp",EDGE,"E4"),sQuery(id+"F4.wireOp",EDGE,"E5")])]}),subQ0,makeQuery(id+"F9.opExtrude","SWEPT_FACE",FACE,{"disambiguationData":[OSD([sQuery(id+"F8.wireOp",EDGE,"E13.1.0.0")])]})])],"derivedFrom":subQ0}),makeQuery(id+"F11.opExtrude","SWEPT_FACE",FACE,{"disambiguationData":[OSD([sQuery(id+"F10.wireOp",EDGE,"E15.0.1.0")])]})]});}
            var Q28;
            Q28=makeQuery(id+"F11.boolean.opBoolean","INTERSECT",EDGE,{"disambiguationData":[OD(0.0)],"derivedFrom":[makeQuery(id+"F9.boolean.opBoolean","COPY",FACE,{"disambiguationData":[OD(0.0)],"derivedFrom":makeQuery(id+"F9.opExtrude","SWEPT_FACE",FACE,{"disambiguationData":[OSD([sQuery(id+"F8.wireOp",EDGE,"E13.1.0.0")])]})}),makeQuery(id+"F11.opExtrude","SWEPT_FACE",FACE,{"disambiguationData":[OSD([sQuery(id+"F10.wireOp",EDGE,"E15.1.1.0")])]})]});
            var Q29;
            {var subQ0=makeQuery(id+"F7.boolean.opBoolean","COPY",FACE,{"derivedFrom":makeQuery(id+"F7.opExtrude","SWEPT_FACE",FACE,{"disambiguationData":[OSD([sQuery(id+"F6.wireOp",EDGE,"E11.1.0.0")])]})});Q29=makeQuery(id+"F11.boolean.opBoolean","INTERSECT",EDGE,{"disambiguationData":[OD(0.0)],"derivedFrom":[makeQuery(id+"F9.boolean.opBoolean","SPLIT",FACE,{"disambiguationData":[TD([makeQuery(id+"F5.opExtrude","SWEPT_FACE",FACE,{"disambiguationData":[OSD([sQuery(id+"F4.wireOp",EDGE,"E3")])]})])],"derivedFrom":subQ0}),makeQuery(id+"F11.opExtrude","SWEPT_FACE",FACE,{"disambiguationData":[OSD([sQuery(id+"F10.wireOp",EDGE,"E15.1.1.0")])]})]});}
            var Q30;
            Q30=makeQuery(id+"F9.boolean.opBoolean","INTERSECT",EDGE,{"disambiguationData":[OD(2.0)],"derivedFrom":[makeQuery(id+"F7.boolean.opBoolean","COPY",FACE,{"derivedFrom":makeQuery(id+"F7.opExtrude","SWEPT_FACE",FACE,{"disambiguationData":[OSD([sQuery(id+"F6.wireOp",EDGE,"E11.1.0.0")])]})}),makeQuery(id+"F9.opExtrude","SWEPT_FACE",FACE,{"disambiguationData":[OSD([sQuery(id+"F8.wireOp",EDGE,"E13.1.0.0")])]})]});
            var Q31;
            {var subQ0=makeQuery(id+"F7.boolean.opBoolean","COPY",FACE,{"derivedFrom":makeQuery(id+"F7.opExtrude","SWEPT_FACE",FACE,{"disambiguationData":[OSD([sQuery(id+"F6.wireOp",EDGE,"E11.1.0.0")])]})});Q31=makeQuery(id+"F11.boolean.opBoolean","INTERSECT",EDGE,{"disambiguationData":[OD(1.0)],"derivedFrom":[makeQuery(id+"F9.boolean.opBoolean","SPLIT",FACE,{"disambiguationData":[TD([makeQuery(id+"F5.opExtrude","SWEPT_FACE",FACE,{"disambiguationData":[OSD([sQuery(id+"F4.wireOp",EDGE,"E3")])]})])],"derivedFrom":subQ0}),makeQuery(id+"F11.opExtrude","SWEPT_FACE",FACE,{"disambiguationData":[OSD([sQuery(id+"F10.wireOp",EDGE,"E15.1.1.0")])]})]});}
            var Q32;
            Q32=makeQuery(id+"F11.boolean.opBoolean","INTERSECT",EDGE,{"disambiguationData":[OD(1.0)],"derivedFrom":[makeQuery(id+"F9.boolean.opBoolean","COPY",FACE,{"disambiguationData":[OD(0.0)],"derivedFrom":makeQuery(id+"F9.opExtrude","SWEPT_FACE",FACE,{"disambiguationData":[OSD([sQuery(id+"F8.wireOp",EDGE,"E13.1.0.0")])]})}),makeQuery(id+"F11.opExtrude","SWEPT_FACE",FACE,{"disambiguationData":[OSD([sQuery(id+"F10.wireOp",EDGE,"E15.1.1.0")])]})]});
            var Q33;
            Q33=makeQuery(id+"F9.boolean.opBoolean","INTERSECT",EDGE,{"disambiguationData":[OD(3.0)],"derivedFrom":[makeQuery(id+"F7.boolean.opBoolean","COPY",FACE,{"derivedFrom":makeQuery(id+"F7.opExtrude","SWEPT_FACE",FACE,{"disambiguationData":[OSD([sQuery(id+"F6.wireOp",EDGE,"E11.1.0.0")])]})}),makeQuery(id+"F9.opExtrude","SWEPT_FACE",FACE,{"disambiguationData":[OSD([sQuery(id+"F8.wireOp",EDGE,"E13.1.0.0")])]})]});
            var Q34;
            Q34=makeQuery(id+"F11.boolean.opBoolean","INTERSECT",EDGE,{"disambiguationData":[OD(0.0)],"derivedFrom":[makeQuery(id+"F9.boolean.opBoolean","COPY",FACE,{"disambiguationData":[OD(2.0)],"derivedFrom":makeQuery(id+"F9.opExtrude","SWEPT_FACE",FACE,{"disambiguationData":[OSD([sQuery(id+"F8.wireOp",EDGE,"E13.1.0.0")])]})}),makeQuery(id+"F11.opExtrude","SWEPT_FACE",FACE,{"disambiguationData":[OSD([sQuery(id+"F10.wireOp",EDGE,"E15.1.1.0")])]})]});
            var Q35;
            Q35=makeQuery(id+"F11.boolean.opBoolean","INTERSECT",EDGE,{"disambiguationData":[OD(1.0)],"derivedFrom":[makeQuery(id+"F9.boolean.opBoolean","COPY",FACE,{"disambiguationData":[OD(2.0)],"derivedFrom":makeQuery(id+"F9.opExtrude","SWEPT_FACE",FACE,{"disambiguationData":[OSD([sQuery(id+"F8.wireOp",EDGE,"E13.1.0.0")])]})}),makeQuery(id+"F11.opExtrude","SWEPT_FACE",FACE,{"disambiguationData":[OSD([sQuery(id+"F10.wireOp",EDGE,"E15.1.1.0")])]})]});
            var Q36;
            Q36=makeQuery(id+"F9.boolean.opBoolean","INTERSECT",EDGE,{"disambiguationData":[OD(1.0)],"derivedFrom":[makeQuery(id+"F7.boolean.opBoolean","COPY",FACE,{"derivedFrom":makeQuery(id+"F7.opExtrude","SWEPT_FACE",FACE,{"disambiguationData":[OSD([sQuery(id+"F6.wireOp",EDGE,"E11.1.0.0")])]})}),makeQuery(id+"F9.opExtrude","SWEPT_FACE",FACE,{"disambiguationData":[OSD([sQuery(id+"F8.wireOp",EDGE,"E13.1.0.0")])]})]});
            var Q37;
            {var subQ0=makeQuery(id+"F7.boolean.opBoolean","COPY",FACE,{"derivedFrom":makeQuery(id+"F7.opExtrude","SWEPT_FACE",FACE,{"disambiguationData":[OSD([sQuery(id+"F6.wireOp",EDGE,"E11.1.0.0")])]})});Q37=makeQuery(id+"F11.boolean.opBoolean","INTERSECT",EDGE,{"disambiguationData":[OD(1.0)],"derivedFrom":[makeQuery(id+"F9.boolean.opBoolean","SPLIT",FACE,{"disambiguationData":[TD([makeQuery(id+"F5.opExtrude","SWEPT_FACE",FACE,{"disambiguationData":[OSD([sQuery(id+"F4.wireOp",EDGE,"E4"),sQuery(id+"F4.wireOp",EDGE,"E5")])]})])],"derivedFrom":subQ0}),makeQuery(id+"F11.opExtrude","SWEPT_FACE",FACE,{"disambiguationData":[OSD([sQuery(id+"F10.wireOp",EDGE,"E15.1.1.0")])]})]});}
            var Q38;
            {var subQ0=makeQuery(id+"F7.boolean.opBoolean","COPY",FACE,{"derivedFrom":makeQuery(id+"F7.opExtrude","SWEPT_FACE",FACE,{"disambiguationData":[OSD([sQuery(id+"F6.wireOp",EDGE,"E11.1.0.0")])]})});Q38=makeQuery(id+"F11.boolean.opBoolean","INTERSECT",EDGE,{"disambiguationData":[OD(0.0)],"derivedFrom":[makeQuery(id+"F9.boolean.opBoolean","SPLIT",FACE,{"disambiguationData":[TD([makeQuery(id+"F5.opExtrude","SWEPT_FACE",FACE,{"disambiguationData":[OSD([sQuery(id+"F4.wireOp",EDGE,"E4"),sQuery(id+"F4.wireOp",EDGE,"E5")])]})])],"derivedFrom":subQ0}),makeQuery(id+"F11.opExtrude","SWEPT_FACE",FACE,{"disambiguationData":[OSD([sQuery(id+"F10.wireOp",EDGE,"E15.1.1.0")])]})]});}
            var Q39;
            Q39=makeQuery(id+"F9.boolean.opBoolean","INTERSECT",EDGE,{"disambiguationData":[OD(0.0)],"derivedFrom":[makeQuery(id+"F7.boolean.opBoolean","COPY",FACE,{"derivedFrom":makeQuery(id+"F7.opExtrude","SWEPT_FACE",FACE,{"disambiguationData":[OSD([sQuery(id+"F6.wireOp",EDGE,"E11.1.0.0")])]})}),makeQuery(id+"F9.opExtrude","SWEPT_FACE",FACE,{"disambiguationData":[OSD([sQuery(id+"F8.wireOp",EDGE,"E13.1.0.0")])]})]});
            var Q40;
            Q40=makeQuery(id+"F9.boolean.opBoolean","INTERSECT",EDGE,{"disambiguationData":[OD(0.0)],"derivedFrom":[makeQuery(id+"F7.boolean.opBoolean","COPY",FACE,{"derivedFrom":makeQuery(id+"F7.opExtrude","SWEPT_FACE",FACE,{"disambiguationData":[OSD([sQuery(id+"F6.wireOp",EDGE,"E9")])]})}),makeQuery(id+"F9.opExtrude","SWEPT_FACE",FACE,{"disambiguationData":[OSD([sQuery(id+"F8.wireOp",EDGE,"E13.1.0.0")])]})]});
            var Q41;
            {var subQ0=makeQuery(id+"F7.boolean.opBoolean","COPY",FACE,{"derivedFrom":makeQuery(id+"F7.opExtrude","SWEPT_FACE",FACE,{"disambiguationData":[OSD([sQuery(id+"F6.wireOp",EDGE,"E9")])]})});Q41=makeQuery(id+"F11.boolean.opBoolean","INTERSECT",EDGE,{"disambiguationData":[OD(0.0)],"derivedFrom":[makeQuery(id+"F9.boolean.opBoolean","SPLIT",FACE,{"disambiguationData":[TD([subQ0,makeQuery(id+"F9.opExtrude","SWEPT_FACE",FACE,{"disambiguationData":[OSD([sQuery(id+"F8.wireOp",EDGE,"E12")])]}),makeQuery(id+"F9.opExtrude","SWEPT_FACE",FACE,{"disambiguationData":[OSD([sQuery(id+"F8.wireOp",EDGE,"E13.1.0.0")])]})])],"derivedFrom":subQ0}),makeQuery(id+"F11.opExtrude","SWEPT_FACE",FACE,{"disambiguationData":[OSD([sQuery(id+"F10.wireOp",EDGE,"E15.0.1.0")])]})]});}
            var Q42;
            Q42=makeQuery(id+"F9.boolean.opBoolean","INTERSECT",EDGE,{"disambiguationData":[OD(3.0)],"derivedFrom":[makeQuery(id+"F7.boolean.opBoolean","COPY",FACE,{"derivedFrom":makeQuery(id+"F7.opExtrude","SWEPT_FACE",FACE,{"disambiguationData":[OSD([sQuery(id+"F6.wireOp",EDGE,"E9")])]})}),makeQuery(id+"F9.opExtrude","SWEPT_FACE",FACE,{"disambiguationData":[OSD([sQuery(id+"F8.wireOp",EDGE,"E13.1.0.0")])]})]});
            var Q43;
            Q43=makeQuery(id+"F9.boolean.opBoolean","INTERSECT",EDGE,{"disambiguationData":[OD(2.0)],"derivedFrom":[makeQuery(id+"F7.boolean.opBoolean","COPY",FACE,{"derivedFrom":makeQuery(id+"F7.opExtrude","SWEPT_FACE",FACE,{"disambiguationData":[OSD([sQuery(id+"F6.wireOp",EDGE,"E9")])]})}),makeQuery(id+"F9.opExtrude","SWEPT_FACE",FACE,{"disambiguationData":[OSD([sQuery(id+"F8.wireOp",EDGE,"E13.1.0.0")])]})]});
            var Q44;
            Q44=makeQuery(id+"F11.boolean.opBoolean","INTERSECT",EDGE,{"disambiguationData":[OD(0.0)],"derivedFrom":[makeQuery(id+"F9.boolean.opBoolean","COPY",FACE,{"disambiguationData":[OD(1.0)],"derivedFrom":makeQuery(id+"F9.opExtrude","SWEPT_FACE",FACE,{"disambiguationData":[OSD([sQuery(id+"F8.wireOp",EDGE,"E13.1.0.0")])]})}),makeQuery(id+"F11.opExtrude","SWEPT_FACE",FACE,{"disambiguationData":[OSD([sQuery(id+"F10.wireOp",EDGE,"E15.0.1.0")])]})]});
            var Q45;
            {var subQ0=makeQuery(id+"F7.boolean.opBoolean","COPY",FACE,{"derivedFrom":makeQuery(id+"F7.opExtrude","SWEPT_FACE",FACE,{"disambiguationData":[OSD([sQuery(id+"F6.wireOp",EDGE,"E9")])]})});Q45=makeQuery(id+"F11.boolean.opBoolean","INTERSECT",EDGE,{"disambiguationData":[OD(1.0)],"derivedFrom":[makeQuery(id+"F9.boolean.opBoolean","SPLIT",FACE,{"disambiguationData":[TD([subQ0,makeQuery(id+"F9.opExtrude","SWEPT_FACE",FACE,{"disambiguationData":[OSD([sQuery(id+"F8.wireOp",EDGE,"E12")])]}),makeQuery(id+"F9.opExtrude","SWEPT_FACE",FACE,{"disambiguationData":[OSD([sQuery(id+"F8.wireOp",EDGE,"E13.1.0.0")])]})])],"derivedFrom":subQ0}),makeQuery(id+"F11.opExtrude","SWEPT_FACE",FACE,{"disambiguationData":[OSD([sQuery(id+"F10.wireOp",EDGE,"E15.0.1.0")])]})]});}
            var Q46;
            Q46=makeQuery(id+"F11.boolean.opBoolean","INTERSECT",EDGE,{"disambiguationData":[OD(1.0)],"derivedFrom":[makeQuery(id+"F9.boolean.opBoolean","COPY",FACE,{"disambiguationData":[OD(1.0)],"derivedFrom":makeQuery(id+"F9.opExtrude","SWEPT_FACE",FACE,{"disambiguationData":[OSD([sQuery(id+"F8.wireOp",EDGE,"E13.1.0.0")])]})}),makeQuery(id+"F11.opExtrude","SWEPT_FACE",FACE,{"disambiguationData":[OSD([sQuery(id+"F10.wireOp",EDGE,"E15.0.1.0")])]})]});
            var Q47;
            Q47=makeQuery(id+"F9.boolean.opBoolean","INTERSECT",EDGE,{"disambiguationData":[OD(0.0)],"derivedFrom":[makeQuery(id+"F7.boolean.opBoolean","COPY",FACE,{"derivedFrom":makeQuery(id+"F7.opExtrude","SWEPT_FACE",FACE,{"disambiguationData":[OSD([sQuery(id+"F6.wireOp",EDGE,"E9")])]})}),makeQuery(id+"F9.opExtrude","SWEPT_FACE",FACE,{"disambiguationData":[OSD([sQuery(id+"F8.wireOp",EDGE,"E12")])]})]});
            var Q48;
            {var subQ0=makeQuery(id+"F7.boolean.opBoolean","COPY",FACE,{"derivedFrom":makeQuery(id+"F7.opExtrude","SWEPT_FACE",FACE,{"disambiguationData":[OSD([sQuery(id+"F6.wireOp",EDGE,"E9")])]})});Q48=makeQuery(id+"F11.boolean.opBoolean","INTERSECT",EDGE,{"disambiguationData":[OD(1.0)],"derivedFrom":[makeQuery(id+"F9.boolean.opBoolean","SPLIT",FACE,{"disambiguationData":[TD([makeQuery(id+"F1.opExtrude","SWEPT_FACE",FACE,{"disambiguationData":[OSD([sQuery(id+"F0.wireOp",EDGE,"E0.bottom")])]}),makeQuery(id+"F3.opExtrude","SWEPT_FACE",FACE,{"disambiguationData":[OSD([sQuery(id+"F2.wireOp",EDGE,"E1.bottom")])]}),makeQuery(id+"F5.opExtrude","SWEPT_FACE",FACE,{"disambiguationData":[OSD([sQuery(id+"F4.wireOp",EDGE,"E8")])]}),subQ0,makeQuery(id+"F9.opExtrude","SWEPT_FACE",FACE,{"disambiguationData":[OSD([sQuery(id+"F8.wireOp",EDGE,"E12")])]})])],"derivedFrom":subQ0}),makeQuery(id+"F11.opExtrude","SWEPT_FACE",FACE,{"disambiguationData":[OSD([sQuery(id+"F10.wireOp",EDGE,"E14")])]})]});}
            var Q49;
            Q49=makeQuery(id+"F9.boolean.opBoolean","INTERSECT",EDGE,{"disambiguationData":[OD(1.0)],"derivedFrom":[makeQuery(id+"F7.boolean.opBoolean","COPY",FACE,{"derivedFrom":makeQuery(id+"F7.opExtrude","SWEPT_FACE",FACE,{"disambiguationData":[OSD([sQuery(id+"F6.wireOp",EDGE,"E9")])]})}),makeQuery(id+"F9.opExtrude","SWEPT_FACE",FACE,{"disambiguationData":[OSD([sQuery(id+"F8.wireOp",EDGE,"E12")])]})]});
            var Q50;
            Q50=makeQuery(id+"F11.boolean.opBoolean","INTERSECT",EDGE,{"disambiguationData":[OD(0.0)],"derivedFrom":[makeQuery(id+"F9.boolean.opBoolean","COPY",FACE,{"disambiguationData":[OD(1.0)],"derivedFrom":makeQuery(id+"F9.opExtrude","SWEPT_FACE",FACE,{"disambiguationData":[OSD([sQuery(id+"F8.wireOp",EDGE,"E12")])]})}),makeQuery(id+"F11.opExtrude","SWEPT_FACE",FACE,{"disambiguationData":[OSD([sQuery(id+"F10.wireOp",EDGE,"E14")])]})]});
            var Q51;
            {var subQ0=makeQuery(id+"F7.boolean.opBoolean","COPY",FACE,{"derivedFrom":makeQuery(id+"F7.opExtrude","SWEPT_FACE",FACE,{"disambiguationData":[OSD([sQuery(id+"F6.wireOp",EDGE,"E9")])]})});Q51=makeQuery(id+"F11.boolean.opBoolean","INTERSECT",EDGE,{"disambiguationData":[OD(0.0)],"derivedFrom":[makeQuery(id+"F9.boolean.opBoolean","SPLIT",FACE,{"disambiguationData":[TD([makeQuery(id+"F1.opExtrude","SWEPT_FACE",FACE,{"disambiguationData":[OSD([sQuery(id+"F0.wireOp",EDGE,"E0.bottom")])]}),makeQuery(id+"F3.opExtrude","SWEPT_FACE",FACE,{"disambiguationData":[OSD([sQuery(id+"F2.wireOp",EDGE,"E1.bottom")])]}),makeQuery(id+"F5.opExtrude","SWEPT_FACE",FACE,{"disambiguationData":[OSD([sQuery(id+"F4.wireOp",EDGE,"E8")])]}),subQ0,makeQuery(id+"F9.opExtrude","SWEPT_FACE",FACE,{"disambiguationData":[OSD([sQuery(id+"F8.wireOp",EDGE,"E12")])]})])],"derivedFrom":subQ0}),makeQuery(id+"F11.opExtrude","SWEPT_FACE",FACE,{"disambiguationData":[OSD([sQuery(id+"F10.wireOp",EDGE,"E14")])]})]});}
            var Q52;
            Q52=makeQuery(id+"F11.boolean.opBoolean","INTERSECT",EDGE,{"disambiguationData":[OD(1.0)],"derivedFrom":[makeQuery(id+"F9.boolean.opBoolean","COPY",FACE,{"disambiguationData":[OD(1.0)],"derivedFrom":makeQuery(id+"F9.opExtrude","SWEPT_FACE",FACE,{"disambiguationData":[OSD([sQuery(id+"F8.wireOp",EDGE,"E12")])]})}),makeQuery(id+"F11.opExtrude","SWEPT_FACE",FACE,{"disambiguationData":[OSD([sQuery(id+"F10.wireOp",EDGE,"E14")])]})]});
            var Q53;
            Q53=makeQuery(id+"F9.boolean.opBoolean","INTERSECT",EDGE,{"disambiguationData":[OD(3.0)],"derivedFrom":[makeQuery(id+"F7.boolean.opBoolean","COPY",FACE,{"derivedFrom":makeQuery(id+"F7.opExtrude","SWEPT_FACE",FACE,{"disambiguationData":[OSD([sQuery(id+"F6.wireOp",EDGE,"E9")])]})}),makeQuery(id+"F9.opExtrude","SWEPT_FACE",FACE,{"disambiguationData":[OSD([sQuery(id+"F8.wireOp",EDGE,"E12")])]})]});
            var Q54;
            Q54=makeQuery(id+"F9.boolean.opBoolean","INTERSECT",EDGE,{"disambiguationData":[OD(0.0)],"derivedFrom":[makeQuery(id+"F7.boolean.opBoolean","COPY",FACE,{"derivedFrom":makeQuery(id+"F7.opExtrude","SWEPT_FACE",FACE,{"disambiguationData":[OSD([sQuery(id+"F6.wireOp",EDGE,"E11.0.1.0")])]})}),makeQuery(id+"F9.opExtrude","SWEPT_FACE",FACE,{"disambiguationData":[OSD([sQuery(id+"F8.wireOp",EDGE,"E13.0.1.0")])]})]});
            var Q55;
            Q55=makeQuery(id+"F11.boolean.opBoolean","INTERSECT",EDGE,{"disambiguationData":[OD(0.0)],"derivedFrom":[makeQuery(id+"F9.boolean.opBoolean","COPY",FACE,{"disambiguationData":[OD(0.0)],"derivedFrom":makeQuery(id+"F9.opExtrude","SWEPT_FACE",FACE,{"disambiguationData":[OSD([sQuery(id+"F8.wireOp",EDGE,"E13.0.1.0")])]})}),makeQuery(id+"F11.opExtrude","SWEPT_FACE",FACE,{"disambiguationData":[OSD([sQuery(id+"F10.wireOp",EDGE,"E14")])]})]});
            var Q56;
            {var subQ0=makeQuery(id+"F7.boolean.opBoolean","COPY",FACE,{"derivedFrom":makeQuery(id+"F7.opExtrude","SWEPT_FACE",FACE,{"disambiguationData":[OSD([sQuery(id+"F6.wireOp",EDGE,"E11.0.1.0")])]})});Q56=makeQuery(id+"F11.boolean.opBoolean","INTERSECT",EDGE,{"disambiguationData":[OD(0.0)],"derivedFrom":[makeQuery(id+"F9.boolean.opBoolean","SPLIT",FACE,{"disambiguationData":[TD([makeQuery(id+"F1.opExtrude","SWEPT_FACE",FACE,{"disambiguationData":[OSD([sQuery(id+"F0.wireOp",EDGE,"E0.bottom")])]})])],"derivedFrom":subQ0}),makeQuery(id+"F11.opExtrude","SWEPT_FACE",FACE,{"disambiguationData":[OSD([sQuery(id+"F10.wireOp",EDGE,"E14")])]})]});}
            var Q57;
            Q57=makeQuery(id+"F11.boolean.opBoolean","INTERSECT",EDGE,{"disambiguationData":[OD(0.0)],"derivedFrom":[makeQuery(id+"F9.boolean.opBoolean","COPY",FACE,{"disambiguationData":[OD(1.0)],"derivedFrom":makeQuery(id+"F9.opExtrude","SWEPT_FACE",FACE,{"disambiguationData":[OSD([sQuery(id+"F8.wireOp",EDGE,"E13.0.1.0")])]})}),makeQuery(id+"F11.opExtrude","SWEPT_FACE",FACE,{"disambiguationData":[OSD([sQuery(id+"F10.wireOp",EDGE,"E14")])]})]});
            var Q58;
            Q58=makeQuery(id+"F9.boolean.opBoolean","INTERSECT",EDGE,{"disambiguationData":[OD(2.0)],"derivedFrom":[makeQuery(id+"F7.boolean.opBoolean","COPY",FACE,{"derivedFrom":makeQuery(id+"F7.opExtrude","SWEPT_FACE",FACE,{"disambiguationData":[OSD([sQuery(id+"F6.wireOp",EDGE,"E11.0.1.0")])]})}),makeQuery(id+"F9.opExtrude","SWEPT_FACE",FACE,{"disambiguationData":[OSD([sQuery(id+"F8.wireOp",EDGE,"E13.0.1.0")])]})]});
            var Q59;
            {var subQ0=makeQuery(id+"F7.boolean.opBoolean","COPY",FACE,{"derivedFrom":makeQuery(id+"F7.opExtrude","SWEPT_FACE",FACE,{"disambiguationData":[OSD([sQuery(id+"F6.wireOp",EDGE,"E11.0.1.0")])]})});Q59=makeQuery(id+"F11.boolean.opBoolean","INTERSECT",EDGE,{"disambiguationData":[OD(0.0)],"derivedFrom":[makeQuery(id+"F9.boolean.opBoolean","SPLIT",FACE,{"disambiguationData":[TD([makeQuery(id+"F1.opExtrude","SWEPT_FACE",FACE,{"disambiguationData":[OSD([sQuery(id+"F0.wireOp",EDGE,"E0.top")])]})])],"derivedFrom":subQ0}),makeQuery(id+"F11.opExtrude","SWEPT_FACE",FACE,{"disambiguationData":[OSD([sQuery(id+"F10.wireOp",EDGE,"E14")])]})]});}
            var Q60;
            Q60=makeQuery(id+"F11.boolean.opBoolean","INTERSECT",EDGE,{"disambiguationData":[OD(1.0)],"derivedFrom":[makeQuery(id+"F9.boolean.opBoolean","COPY",FACE,{"disambiguationData":[OD(0.0)],"derivedFrom":makeQuery(id+"F9.opExtrude","SWEPT_FACE",FACE,{"disambiguationData":[OSD([sQuery(id+"F8.wireOp",EDGE,"E13.0.1.0")])]})}),makeQuery(id+"F11.opExtrude","SWEPT_FACE",FACE,{"disambiguationData":[OSD([sQuery(id+"F10.wireOp",EDGE,"E14")])]})]});
            var Q61;
            {var subQ0=makeQuery(id+"F7.boolean.opBoolean","COPY",FACE,{"derivedFrom":makeQuery(id+"F7.opExtrude","SWEPT_FACE",FACE,{"disambiguationData":[OSD([sQuery(id+"F6.wireOp",EDGE,"E11.0.1.0")])]})});Q61=makeQuery(id+"F11.boolean.opBoolean","INTERSECT",EDGE,{"disambiguationData":[OD(1.0)],"derivedFrom":[makeQuery(id+"F9.boolean.opBoolean","SPLIT",FACE,{"disambiguationData":[TD([makeQuery(id+"F1.opExtrude","SWEPT_FACE",FACE,{"disambiguationData":[OSD([sQuery(id+"F0.wireOp",EDGE,"E0.top")])]})])],"derivedFrom":subQ0}),makeQuery(id+"F11.opExtrude","SWEPT_FACE",FACE,{"disambiguationData":[OSD([sQuery(id+"F10.wireOp",EDGE,"E14")])]})]});}
            var Q62;
            Q62=makeQuery(id+"F9.boolean.opBoolean","INTERSECT",EDGE,{"disambiguationData":[OD(3.0)],"derivedFrom":[makeQuery(id+"F7.boolean.opBoolean","COPY",FACE,{"derivedFrom":makeQuery(id+"F7.opExtrude","SWEPT_FACE",FACE,{"disambiguationData":[OSD([sQuery(id+"F6.wireOp",EDGE,"E11.0.1.0")])]})}),makeQuery(id+"F9.opExtrude","SWEPT_FACE",FACE,{"disambiguationData":[OSD([sQuery(id+"F8.wireOp",EDGE,"E13.0.1.0")])]})]});
            var Q63;
            Q63=makeQuery(id+"F9.boolean.opBoolean","INTERSECT",EDGE,{"disambiguationData":[OD(2.0)],"derivedFrom":[makeQuery(id+"F7.boolean.opBoolean","COPY",FACE,{"derivedFrom":makeQuery(id+"F7.opExtrude","SWEPT_FACE",FACE,{"disambiguationData":[OSD([sQuery(id+"F6.wireOp",EDGE,"E11.0.2.0")])]})}),makeQuery(id+"F9.opExtrude","SWEPT_FACE",FACE,{"disambiguationData":[OSD([sQuery(id+"F8.wireOp",EDGE,"E13.0.2.0")])]})]});
            var Q64;
            {var subQ0=makeQuery(id+"F7.boolean.opBoolean","COPY",FACE,{"derivedFrom":makeQuery(id+"F7.opExtrude","SWEPT_FACE",FACE,{"disambiguationData":[OSD([sQuery(id+"F6.wireOp",EDGE,"E11.0.2.0")])]})});Q64=makeQuery(id+"F11.boolean.opBoolean","INTERSECT",EDGE,{"disambiguationData":[OD(0.0)],"derivedFrom":[makeQuery(id+"F9.boolean.opBoolean","SPLIT",FACE,{"disambiguationData":[TD([makeQuery(id+"F1.opExtrude","SWEPT_FACE",FACE,{"disambiguationData":[OSD([sQuery(id+"F0.wireOp",EDGE,"E0.top")])]})])],"derivedFrom":subQ0}),makeQuery(id+"F11.opExtrude","SWEPT_FACE",FACE,{"disambiguationData":[OSD([sQuery(id+"F10.wireOp",EDGE,"E14")])]})]});}
            var Q65;
            Q65=makeQuery(id+"F11.boolean.opBoolean","INTERSECT",EDGE,{"disambiguationData":[OD(1.0)],"derivedFrom":[makeQuery(id+"F9.boolean.opBoolean","COPY",FACE,{"disambiguationData":[OD(1.0)],"derivedFrom":makeQuery(id+"F9.opExtrude","SWEPT_FACE",FACE,{"disambiguationData":[OSD([sQuery(id+"F8.wireOp",EDGE,"E13.0.2.0")])]})}),makeQuery(id+"F11.opExtrude","SWEPT_FACE",FACE,{"disambiguationData":[OSD([sQuery(id+"F10.wireOp",EDGE,"E14")])]})]});
            var Q66;
            {var subQ0=makeQuery(id+"F7.boolean.opBoolean","COPY",FACE,{"derivedFrom":makeQuery(id+"F7.opExtrude","SWEPT_FACE",FACE,{"disambiguationData":[OSD([sQuery(id+"F6.wireOp",EDGE,"E11.0.2.0")])]})});Q66=makeQuery(id+"F11.boolean.opBoolean","INTERSECT",EDGE,{"disambiguationData":[OD(1.0)],"derivedFrom":[makeQuery(id+"F9.boolean.opBoolean","SPLIT",FACE,{"disambiguationData":[TD([makeQuery(id+"F1.opExtrude","SWEPT_FACE",FACE,{"disambiguationData":[OSD([sQuery(id+"F0.wireOp",EDGE,"E0.top")])]})])],"derivedFrom":subQ0}),makeQuery(id+"F11.opExtrude","SWEPT_FACE",FACE,{"disambiguationData":[OSD([sQuery(id+"F10.wireOp",EDGE,"E14")])]})]});}
            var Q67;
            Q67=makeQuery(id+"F9.boolean.opBoolean","INTERSECT",EDGE,{"disambiguationData":[OD(3.0)],"derivedFrom":[makeQuery(id+"F7.boolean.opBoolean","COPY",FACE,{"derivedFrom":makeQuery(id+"F7.opExtrude","SWEPT_FACE",FACE,{"disambiguationData":[OSD([sQuery(id+"F6.wireOp",EDGE,"E11.0.2.0")])]})}),makeQuery(id+"F9.opExtrude","SWEPT_FACE",FACE,{"disambiguationData":[OSD([sQuery(id+"F8.wireOp",EDGE,"E13.0.2.0")])]})]});
            var Q68;
            Q68=makeQuery(id+"F11.boolean.opBoolean","INTERSECT",EDGE,{"disambiguationData":[OD(1.0)],"derivedFrom":[makeQuery(id+"F9.boolean.opBoolean","COPY",FACE,{"disambiguationData":[OD(2.0)],"derivedFrom":makeQuery(id+"F9.opExtrude","SWEPT_FACE",FACE,{"disambiguationData":[OSD([sQuery(id+"F8.wireOp",EDGE,"E13.0.2.0")])]})}),makeQuery(id+"F11.opExtrude","SWEPT_FACE",FACE,{"disambiguationData":[OSD([sQuery(id+"F10.wireOp",EDGE,"E14")])]})]});
            var Q69;
            Q69=makeQuery(id+"F9.boolean.opBoolean","INTERSECT",EDGE,{"disambiguationData":[OD(1.0)],"derivedFrom":[makeQuery(id+"F7.boolean.opBoolean","COPY",FACE,{"derivedFrom":makeQuery(id+"F7.opExtrude","SWEPT_FACE",FACE,{"disambiguationData":[OSD([sQuery(id+"F6.wireOp",EDGE,"E11.0.2.0")])]})}),makeQuery(id+"F9.opExtrude","SWEPT_FACE",FACE,{"disambiguationData":[OSD([sQuery(id+"F8.wireOp",EDGE,"E13.0.2.0")])]})]});
            var Q70;
            {var subQ0=makeQuery(id+"F7.boolean.opBoolean","COPY",FACE,{"derivedFrom":makeQuery(id+"F7.opExtrude","SWEPT_FACE",FACE,{"disambiguationData":[OSD([sQuery(id+"F6.wireOp",EDGE,"E11.0.2.0")])]})});Q70=makeQuery(id+"F11.boolean.opBoolean","INTERSECT",EDGE,{"disambiguationData":[OD(1.0)],"derivedFrom":[makeQuery(id+"F9.boolean.opBoolean","SPLIT",FACE,{"disambiguationData":[TD([makeQuery(id+"F1.opExtrude","SWEPT_FACE",FACE,{"disambiguationData":[OSD([sQuery(id+"F0.wireOp",EDGE,"E0.bottom")])]})])],"derivedFrom":subQ0}),makeQuery(id+"F11.opExtrude","SWEPT_FACE",FACE,{"disambiguationData":[OSD([sQuery(id+"F10.wireOp",EDGE,"E14")])]})]});}
            var Q71;
            Q71=makeQuery(id+"F11.boolean.opBoolean","INTERSECT",EDGE,{"disambiguationData":[OD(0.0)],"derivedFrom":[makeQuery(id+"F9.boolean.opBoolean","COPY",FACE,{"disambiguationData":[OD(2.0)],"derivedFrom":makeQuery(id+"F9.opExtrude","SWEPT_FACE",FACE,{"disambiguationData":[OSD([sQuery(id+"F8.wireOp",EDGE,"E13.0.2.0")])]})}),makeQuery(id+"F11.opExtrude","SWEPT_FACE",FACE,{"disambiguationData":[OSD([sQuery(id+"F10.wireOp",EDGE,"E14")])]})]});
            fillet(context, id + "F15", {"entities" : qUnion([Q0, Q1, Q2, Q3, Q4, Q5, Q6, Q7, Q8, Q9, Q10, Q11, Q12, Q13, Q14, Q15, Q16, Q17, Q18, Q19, Q20, Q21, Q22, Q23, Q24, Q25, Q26, Q27, Q28, Q29, Q30, Q31, Q32, Q33, Q34, Q35, Q36, Q37, Q38, Q39, Q40, Q41, Q42, Q43, Q44, Q45, Q46, Q47, Q48, Q49, Q50, Q51, Q52, Q53, Q54, Q55, Q56, Q57, Q58, Q59, Q60, Q61, Q62, Q63, Q64, Q65, Q66, Q67, Q68, Q69, Q70, Q71]), "radius" : 2.54 * mm, "tangentPropagation" : true, "allowEdgeOverflow" : false});
        }
    });
